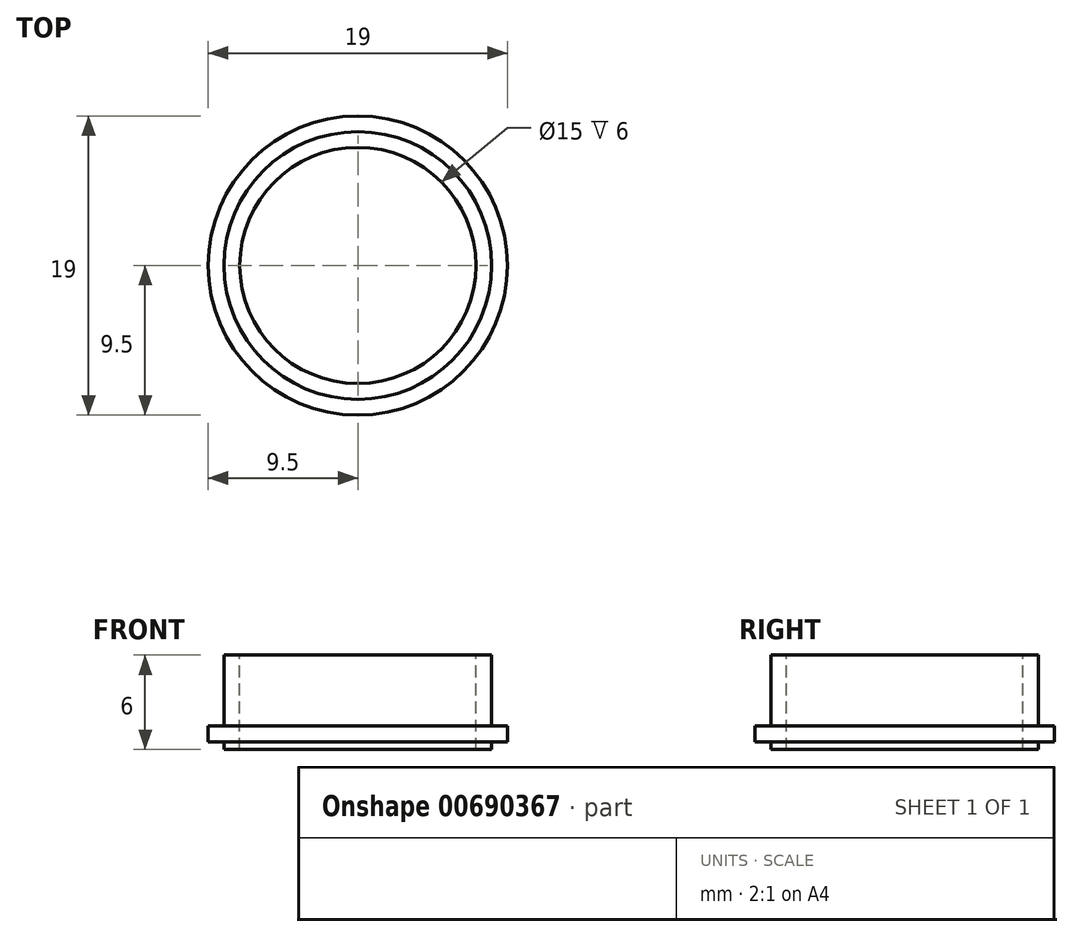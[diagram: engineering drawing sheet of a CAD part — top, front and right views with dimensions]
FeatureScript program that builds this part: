
annotation { "Feature Type Name" : "Feature", "Feature Type Description" : "" }
export const myFeature = defineFeature(function(context is Context, id is Id, definition is map)
    precondition{}
    {
        {
            var Q0;
            Q0=qCreatedBy(makeId("Front.planeOp"),FACE);
            var sketch = newSketch(context, id + "F0", { "sketchPlane" : qUnion([Q0])});
            skLineSegment(sketch, "E0", {"start": v(0, 8.37) * mm, "end": v(0, -6.17) * mm, "construction": true});
            skLineSegment(sketch, "E1", {"start": v(-7.5, 0) * mm, "end": v(-7.5, 6) * mm});
            skLineSegment(sketch, "E2", {"start": v(-7.5, 6) * mm, "end": v(-8.5, 6) * mm});
            skLineSegment(sketch, "E3", {"start": v(-8.5, 6) * mm, "end": v(-8.5, 1.5) * mm});
            skLineSegment(sketch, "E4", {"start": v(-8.5, 1.5) * mm, "end": v(-9.5, 1.5) * mm});
            skLineSegment(sketch, "E5", {"start": v(-9.5, 1.5) * mm, "end": v(-9.5, 0.5) * mm});
            skLineSegment(sketch, "E6", {"start": v(-9.5, 0.5) * mm, "end": v(-8.5, 0.5) * mm});
            skLineSegment(sketch, "E7", {"start": v(-8.5, 0.5) * mm, "end": v(-8.5, 0) * mm});
            skLineSegment(sketch, "E8", {"start": v(-8.5, 0) * mm, "end": v(-7.5, 0) * mm});
            skSolve(sketch);
        }
        {
            var Q0;
            Q0 = qSketchRegion(id + "F0", true);
            var Q1;
            Q1=sQuery(id+"F0.wireOp",EDGE,"E0");
            revolve(context, id + "F1", {"entities" : qUnion([Q0]), "axis" : qUnion([Q1]), "revolveType" : RevolveType.FULL});
        }
    });
